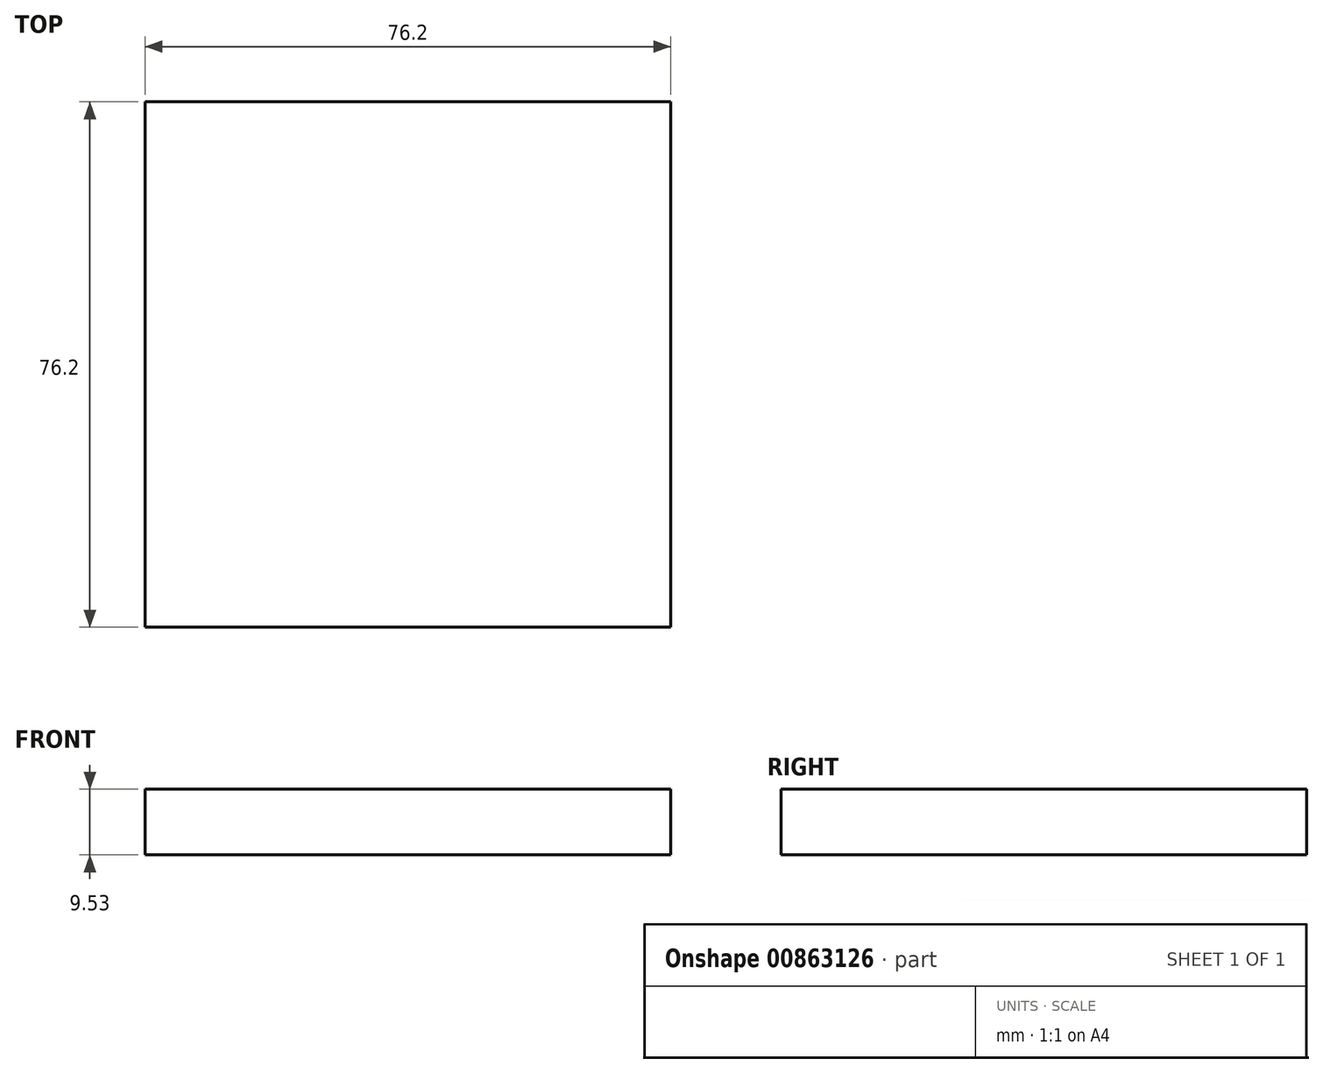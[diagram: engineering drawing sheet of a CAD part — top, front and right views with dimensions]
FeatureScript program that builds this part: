
annotation { "Feature Type Name" : "Feature", "Feature Type Description" : "" }
export const myFeature = defineFeature(function(context is Context, id is Id, definition is map)
    precondition{}
    {
        {
            var Q0;
            Q0=qCreatedBy(makeId("Right.planeOp"),FACE);
            var sketch = newSketch(context, id + "F0", { "sketchPlane" : qUnion([Q0])});
            skLineSegment(sketch, "E0.bottom", {"start": v(-34.96, -4.59) * mm, "end": v(41.24, -4.59) * mm});
            skLineSegment(sketch, "E0.top", {"start": v(-34.96, 4.94) * mm, "end": v(41.24, 4.94) * mm});
            skLineSegment(sketch, "E0.left", {"start": v(-34.96, -4.59) * mm, "end": v(-34.96, 4.94) * mm});
            skLineSegment(sketch, "E0.right", {"start": v(41.24, -4.59) * mm, "end": v(41.24, 4.94) * mm});
            skSolve(sketch);
        }
        {
            var Q0;
            Q0 = qSketchRegion(id + "F0", true);
            extrude(context, id + "F1", {"entities" : qUnion([Q0]), "depth" : 76.2 * mm, "offsetDistance" : 25.4 * mm});
        }
    });
